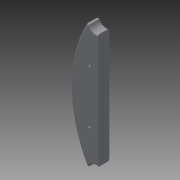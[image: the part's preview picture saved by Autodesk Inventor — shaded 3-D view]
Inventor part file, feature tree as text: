
AUTODESK INVENTOR PART (.ipt)
format: ipt  version: 2015 (Build 190159000, 159)  size: 127,488 bytes
history: native  units: mm
features: fillet x2, extrude x1, sketch x1
ambient origin geometry x8: Origin, YZ Plane, XZ Plane, XY Plane, X Axis, Y Axis, Z Axis, Center Point
bodies: Body1 (feature_tree)
feature tree (4):
  extrude  "Extrusion5"  Depth=2.0mm
  fillet  "Fillet1"  Radius=3.0mm
  fillet  "Fillet2"  Radius=3.0mm
  sketch  "Sketch1"  dims[d13=35.0mm d14=35.35mm d17=3.0mm d21=3.0mm d24=31.0mm d27=65.5mm d28=65.5mm d35=14.0mm d36=8.0mm d37=14.0mm d38=8.0mm d39=13.0mm d40=0.0mm d41=2.0mm d42=2.0mm]
